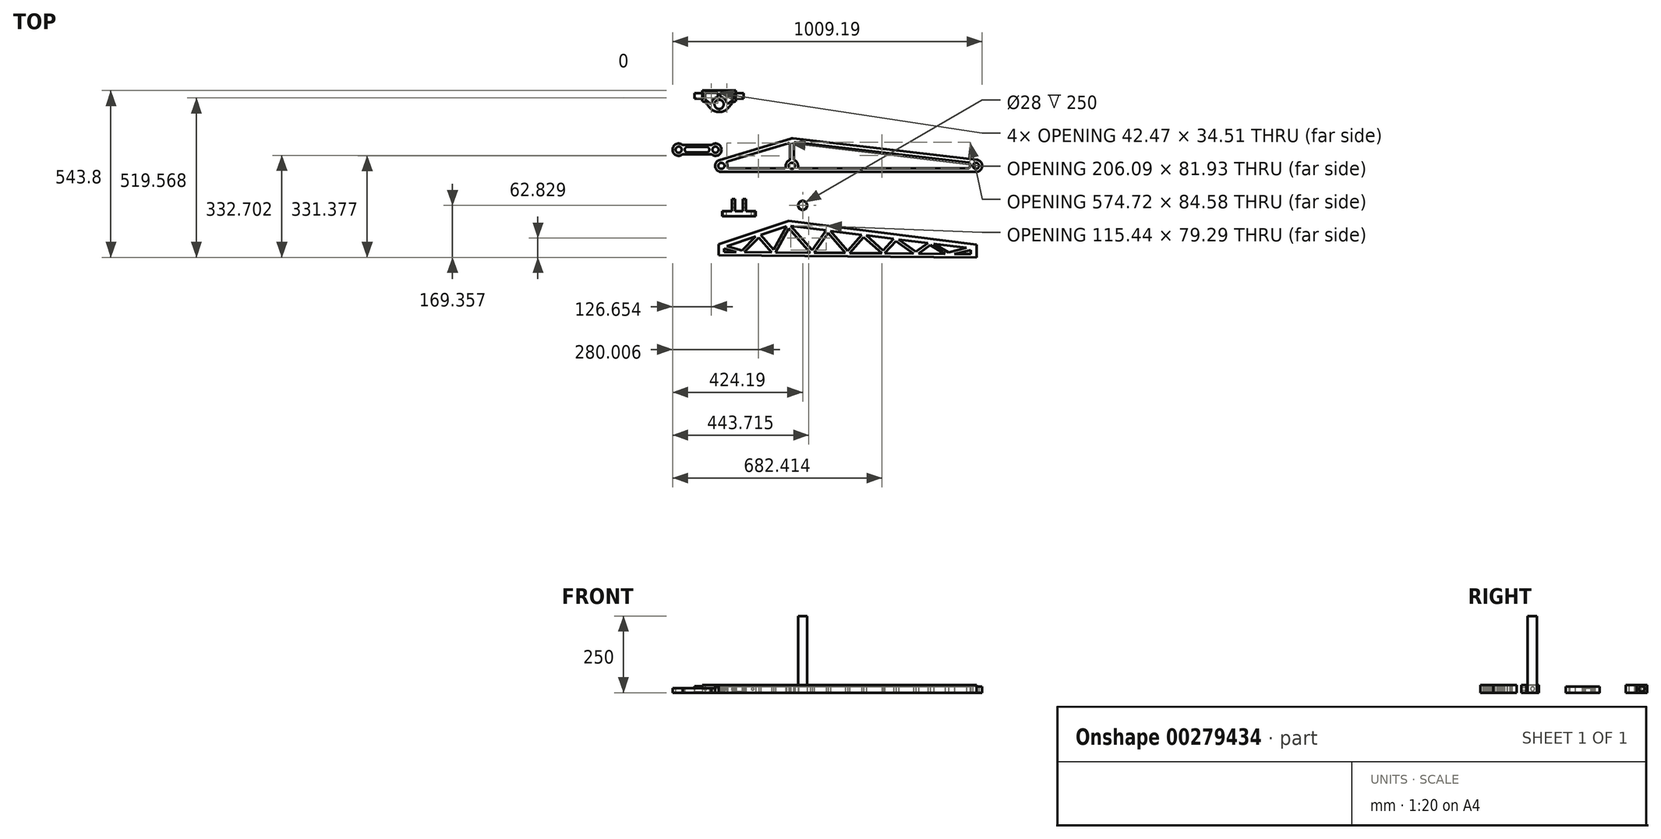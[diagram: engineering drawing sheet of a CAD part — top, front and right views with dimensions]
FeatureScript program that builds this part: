
annotation { "Feature Type Name" : "Feature", "Feature Type Description" : "" }
export const myFeature = defineFeature(function(context is Context, id is Id, definition is map)
    precondition{}
    {
        {
            var Q0;
            Q0=qCreatedBy(makeId("Top.planeOp"),FACE);
            var sketch = newSketch(context, id + "F0", { "sketchPlane" : qUnion([Q0])});
            skCircle(sketch, "E0", {"center": v(-265.14, 0) * mm, "radius": 10 * mm});
            skCircle(sketch, "E1", {"center": v(-35.14, 0) * mm, "radius": 10 * mm});
            skCircle(sketch, "E2", {"center": v(564.86, 0) * mm, "radius": 10 * mm});
            skLineSegment(sketch, "E3", {"start": v(-31.03, 89.52) * mm, "end": v(567.19, 20) * mm});
            skLineSegment(sketch, "E4", {"start": v(567.19, -20) * mm, "end": v(-265.14, -20) * mm});
            skArc(sketch, "E5", {"start": v(-265.14, -20) * mm, "mid": v(-284.92, -2.9) * mm, "end": v(-270.9, 19.15) * mm});
            skLineSegment(sketch, "E6", {"start": v(-270.9, 19.15) * mm, "end": v(-39.1, 88.81) * mm});
            skArc(sketch, "E7", {"start": v(567.19, -20) * mm, "mid": v(585, 0) * mm, "end": v(567.19, 20) * mm});
            skPoint(sketch, "E8.visualSharp", {"position": v(-35.14, 90) * mm});
            skArc(sketch, "E8.filletArc", {"start": v(-31.03, 89.52) * mm, "mid": v(-35.1, 89.58) * mm, "end": v(-39.1, 88.81) * mm});
            skLineSegment(sketch, "E9", {"start": v(-249.89, 12.94) * mm, "end": v(-41.14, 75.67) * mm});
            skLineSegment(sketch, "E10", {"start": v(-41.14, 75.67) * mm, "end": v(-249.89, 12.94) * mm});
            skLineSegment(sketch, "E11", {"start": v(-246.8, -8) * mm, "end": v(-53.47, -8) * mm});
            skLineSegment(sketch, "E12", {"start": v(-89.9, -8) * mm, "end": v(-89.9, -20) * mm, "construction": true});
            skLineSegment(sketch, "E13", {"start": v(-87.57, 61.71) * mm, "end": v(-91.02, 73.2) * mm, "construction": true});
            skLineSegment(sketch, "E14", {"start": v(-35.14, 0) * mm, "end": v(-35.14, 166.99) * mm, "construction": true});
            skLineSegment(sketch, "E15", {"start": v(-53.47, -8) * mm, "end": v(-35.14, -8) * mm, "construction": true});
            skLineSegment(sketch, "E16", {"start": v(-35.14, -8) * mm, "end": v(-16.8, -8) * mm, "construction": true});
            skLineSegment(sketch, "E17", {"start": v(-29.14, 19.08) * mm, "end": v(-29.14, 77.22) * mm});
            skLineSegment(sketch, "E18", {"start": v(-41.14, 17.52) * mm, "end": v(-29.14, 17.52) * mm, "construction": true});
            skLineSegment(sketch, "E19", {"start": v(-29.14, 77.22) * mm, "end": v(547.65, 10.19) * mm});
            skLineSegment(sketch, "E20", {"start": v(-9, 74.88) * mm, "end": v(-7.6, 86.8) * mm, "construction": true});
            skLineSegment(sketch, "E21", {"start": v(-16.8, -8) * mm, "end": v(546.53, -8) * mm});
            skArc(sketch, "E22", {"start": v(547.65, 10.19) * mm, "mid": v(544.9, 1.23) * mm, "end": v(546.53, -8) * mm});
            skArc(sketch, "E23", {"start": v(-246.8, -8) * mm, "mid": v(-245.35, 2.9) * mm, "end": v(-249.89, 12.94) * mm});
            skArc(sketch, "E24", {"start": v(-16.8, -8) * mm, "mid": v(-35.14, 20) * mm, "end": v(-53.47, -8) * mm});
            skLineSegment(sketch, "E25", {"start": v(-41.14, 75.67) * mm, "end": v(-41.14, 19.08) * mm});
            skLineSegment(sketch, "E26", {"start": v(-41.14, 40.34) * mm, "end": v(-35.14, 40.34) * mm, "construction": true});
            skLineSegment(sketch, "E27", {"start": v(-35.14, 40.34) * mm, "end": v(-29.14, 40.34) * mm, "construction": true});
            skSolve(sketch);
        }
        {
            var Q0;
            Q0 = qSketchRegion(id + "F0", true);
            extrude(context, id + "F1", {"entities" : qUnion([Q0]), "depth" : 20 * mm});
        }
        {
            var Q0;
            Q0=makeQuery(id+"F1.opExtrude","SWEPT_EDGE",EDGE,{"disambiguationData":[OSD([sQuery(id+"F0.wireOp",EDGE,"E19"),sQuery(id+"F0.wireOp",EDGE,"E22")])]});
            var Q1;
            Q1=makeQuery(id+"F1.opExtrude","SWEPT_EDGE",EDGE,{"disambiguationData":[OSD([sQuery(id+"F0.wireOp",EDGE,"E21"),sQuery(id+"F0.wireOp",EDGE,"E22")])]});
            var Q2;
            Q2=makeQuery(id+"F1.opExtrude","SWEPT_EDGE",EDGE,{"disambiguationData":[OSD([sQuery(id+"F0.wireOp",EDGE,"E17"),sQuery(id+"F0.wireOp",EDGE,"E19")])]});
            var Q3;
            Q3=makeQuery(id+"F1.opExtrude","SWEPT_EDGE",EDGE,{"disambiguationData":[OSD([sQuery(id+"F0.wireOp",EDGE,"E17"),sQuery(id+"F0.wireOp",EDGE,"E24")])]});
            var Q4;
            Q4=makeQuery(id+"F1.opExtrude","SWEPT_EDGE",EDGE,{"disambiguationData":[OSD([sQuery(id+"F0.wireOp",EDGE,"E21"),sQuery(id+"F0.wireOp",EDGE,"E24")])]});
            var Q5;
            Q5=makeQuery(id+"F1.opExtrude","SWEPT_EDGE",EDGE,{"disambiguationData":[OSD([sQuery(id+"F0.wireOp",EDGE,"E11"),sQuery(id+"F0.wireOp",EDGE,"E24")])]});
            var Q6;
            Q6=makeQuery(id+"F1.opExtrude","SWEPT_EDGE",EDGE,{"disambiguationData":[OSD([sQuery(id+"F0.wireOp",EDGE,"E24"),sQuery(id+"F0.wireOp",EDGE,"E25")])]});
            var Q7;
            Q7=makeQuery(id+"F1.opExtrude","SWEPT_EDGE",EDGE,{"disambiguationData":[OSD([sQuery(id+"F0.wireOp",EDGE,"E10"),sQuery(id+"F0.wireOp",EDGE,"E25")])]});
            var Q8;
            Q8=makeQuery(id+"F1.opExtrude","SWEPT_EDGE",EDGE,{"disambiguationData":[OSD([sQuery(id+"F0.wireOp",EDGE,"E11"),sQuery(id+"F0.wireOp",EDGE,"E23")])]});
            var Q9;
            Q9=makeQuery(id+"F1.opExtrude","SWEPT_EDGE",EDGE,{"disambiguationData":[OSD([sQuery(id+"F0.wireOp",EDGE,"E10"),sQuery(id+"F0.wireOp",EDGE,"E23")])]});
            fillet(context, id + "F2", {"entities" : qUnion([Q0, Q1, Q2, Q3, Q4, Q5, Q6, Q7, Q8, Q9]), "radius" : 5 * mm, "tangentPropagation" : true, "allowEdgeOverflow" : false});
        }
        {
            var Q0;
            Q0=qCreatedBy(makeId("Top.planeOp"),FACE);
            var sketch = newSketch(context, id + "F3", { "sketchPlane" : qUnion([Q0])});
            skLineSegment(sketch, "E28", {"start": v(-390.96, 67.67) * mm, "end": v(-297.41, 67.67) * mm});
            skLineSegment(sketch, "E29", {"start": v(-297.41, 37.67) * mm, "end": v(-390.96, 37.67) * mm});
            skArc(sketch, "E30", {"start": v(-297.41, 37.67) * mm, "mid": v(-264.19, 52.67) * mm, "end": v(-297.41, 67.67) * mm});
            skArc(sketch, "E31", {"start": v(-390.96, 67.67) * mm, "mid": v(-424.19, 52.67) * mm, "end": v(-390.96, 37.67) * mm});
            skPoint(sketch, "E32.orphan", {"position": v(-404.19, 67.67) * mm});
            skPoint(sketch, "E33.orphan", {"position": v(-404.19, 37.67) * mm});
            skPoint(sketch, "E34.orphan", {"position": v(-284.19, 37.67) * mm});
            skPoint(sketch, "E35.orphan", {"position": v(-284.19, 67.67) * mm});
            skCircle(sketch, "E36", {"center": v(-404.19, 52.67) * mm, "radius": 10 * mm});
            skCircle(sketch, "E37", {"center": v(-284.19, 52.67) * mm, "radius": 10 * mm});
            skLineSegment(sketch, "E38", {"start": v(-404.19, 52.67) * mm, "end": v(-284.19, 52.67) * mm, "construction": true});
            skLineSegment(sketch, "E39", {"start": v(-375.19, 61.67) * mm, "end": v(-313.19, 61.67) * mm});
            skArc(sketch, "E40", {"start": v(-375.19, 61.67) * mm, "mid": v(-384.19, 52.67) * mm, "end": v(-375.19, 43.67) * mm});
            skLineSegment(sketch, "E41", {"start": v(-375.19, 43.67) * mm, "end": v(-313.19, 43.67) * mm});
            skArc(sketch, "E42", {"start": v(-313.19, 61.67) * mm, "mid": v(-304.19, 52.67) * mm, "end": v(-313.19, 43.67) * mm});
            skSolve(sketch);
        }
        {
            var Q0;
            Q0 = qSketchRegion(id + "F3", true);
            extrude(context, id + "F4", {"entities" : qUnion([Q0]), "depth" : 15 * mm});
        }
        {
            var Q0;
            Q0=qCreatedBy(makeId("Top.planeOp"),FACE);
            var sketch = newSketch(context, id + "F5", { "sketchPlane" : qUnion([Q0])});
            skLineSegment(sketch, "E43", {"start": v(-327.3, 245.39) * mm, "end": v(-217.3, 245.39) * mm});
            skLineSegment(sketch, "E44", {"start": v(-217.3, 245.39) * mm, "end": v(-217.3, 210.39) * mm});
            skLineSegment(sketch, "E45", {"start": v(-327.3, 210.39) * mm, "end": v(-327.3, 245.39) * mm});
            skCircle(sketch, "E46", {"center": v(-272.3, 200.39) * mm, "radius": 15 * mm});
            skPoint(sketch, "E46.centerSnap0", {"position": v(-272.3, 175.39) * mm});
            skCircle(sketch, "E47", {"center": v(-272.3, 200.39) * mm, "radius": 25 * mm, "construction": true});
            skFitSpline(sketch, "E48", {"points": [v(-327.3, 210.39) * mm, v(-272.3, 175.39) * mm], "startDerivative": vector(60, 0) * mm, "endDerivative": vector(105, 0) * mm});
            skLineSegment(sketch, "E49", {"start": v(-272.3, 200.39) * mm, "end": v(-272.3, 245.39) * mm, "construction": true});
            skLineSegment(sketch, "E50", {"start": v(-327.3, 245.39) * mm, "end": v(-272.3, 200.39) * mm, "construction": true});
            skLineSegment(sketch, "E51", {"start": v(-272.3, 200.39) * mm, "end": v(-217.3, 245.39) * mm, "construction": true});
            skLineSegment(sketch, "E52", {"start": v(-327.3, 210.39) * mm, "end": v(-217.3, 210.39) * mm, "construction": true});
            skFitSpline(sketch, "E53.MirrorCS", {"points": [v(-217.3, 210.39) * mm, v(-272.3, 175.39) * mm], "startDerivative": vector(-60, 0) * mm, "endDerivative": vector(-105, 0) * mm});
            skLineSegment(sketch, "E54", {"start": v(-281.3, 238.41) * mm, "end": v(-313.77, 238.41) * mm});
            skLineSegment(sketch, "E55", {"start": v(-318.77, 233.41) * mm, "end": v(-318.77, 220.85) * mm});
            skLineSegment(sketch, "E56", {"start": v(-317.2, 217.2) * mm, "end": v(-304.5, 205.26) * mm});
            skArc(sketch, "E57", {"start": v(-296.27, 207.48) * mm, "mid": v(-287.26, 220.42) * mm, "end": v(-272.3, 225.39) * mm});
            skPoint(sketch, "E58.visualSharp", {"position": v(-318.77, 238.41) * mm});
            skArc(sketch, "E58.filletArc", {"start": v(-313.77, 238.41) * mm, "mid": v(-317.3, 236.95) * mm, "end": v(-318.77, 233.41) * mm});
            skPoint(sketch, "E59.visualSharp", {"position": v(-318.77, 218.69) * mm});
            skArc(sketch, "E59.filletArc", {"start": v(-318.77, 220.85) * mm, "mid": v(-318.36, 218.86) * mm, "end": v(-317.2, 217.2) * mm});
            skArc(sketch, "E60.MirrorCS", {"start": v(-230.83, 238.41) * mm, "mid": v(-227.3, 236.95) * mm, "end": v(-225.83, 233.41) * mm});
            skLineSegment(sketch, "E61.MirrorCS", {"start": v(-225.83, 233.41) * mm, "end": v(-225.83, 220.85) * mm});
            skLineSegment(sketch, "E62.MirrorCS", {"start": v(-227.4, 217.2) * mm, "end": v(-240.1, 205.26) * mm});
            skPoint(sketch, "E63.MirrorP", {"position": v(-225.83, 218.69) * mm});
            skArc(sketch, "E64.MirrorCS", {"start": v(-225.83, 220.85) * mm, "mid": v(-226.24, 218.86) * mm, "end": v(-227.4, 217.2) * mm});
            skArc(sketch, "E65.MirrorCS", {"start": v(-248.33, 207.48) * mm, "mid": v(-257.34, 220.42) * mm, "end": v(-272.3, 225.39) * mm});
            skPoint(sketch, "E66.visualSharp", {"position": v(-297.22, 198.43) * mm});
            skArc(sketch, "E66.filletArc", {"start": v(-304.5, 205.26) * mm, "mid": v(-299.76, 204.08) * mm, "end": v(-296.27, 207.48) * mm});
            skPoint(sketch, "E67.visualSharp", {"position": v(-247.38, 198.43) * mm});
            skArc(sketch, "E67.filletArc", {"start": v(-248.33, 207.48) * mm, "mid": v(-244.84, 204.08) * mm, "end": v(-240.1, 205.26) * mm});
            skLineSegment(sketch, "E68", {"start": v(-276.3, 233.41) * mm, "end": v(-276.3, 229.73) * mm});
            skPoint(sketch, "E69.orphan", {"position": v(-272.3, 238.41) * mm});
            skPoint(sketch, "E70.MirrorCS.end.orphan", {"position": v(-230.83, 238.41) * mm});
            skLineSegment(sketch, "E71.MirrorCS", {"start": v(-268.3, 233.41) * mm, "end": v(-268.3, 229.73) * mm});
            skLineSegment(sketch, "E72.MirrorCS", {"start": v(-263.3, 238.41) * mm, "end": v(-230.83, 238.41) * mm});
            skPoint(sketch, "E73.visualSharp", {"position": v(-276.3, 238.41) * mm});
            skArc(sketch, "E73.filletArc", {"start": v(-276.3, 233.41) * mm, "mid": v(-277.76, 236.95) * mm, "end": v(-281.3, 238.41) * mm});
            skPoint(sketch, "E74.visualSharp", {"position": v(-268.3, 238.41) * mm});
            skArc(sketch, "E74.filletArc", {"start": v(-263.3, 238.41) * mm, "mid": v(-266.84, 236.95) * mm, "end": v(-268.3, 233.41) * mm});
            skArc(sketch, "E75", {"start": v(-280.37, 224.05) * mm, "mid": v(-277.42, 226.24) * mm, "end": v(-276.3, 229.73) * mm});
            skPoint(sketch, "E76.orphan", {"position": v(-276.3, 225.07) * mm});
            skArc(sketch, "E77.MirrorCS", {"start": v(-264.23, 224.05) * mm, "mid": v(-267.18, 226.24) * mm, "end": v(-268.3, 229.73) * mm});
            skPoint(sketch, "E78.orphan", {"position": v(-268.3, 225.07) * mm});
            skSolve(sketch);
        }
        {
            var Q0;
            Q0 = qSketchRegion(id + "F5", true);
            extrude(context, id + "F6", {"entities" : qUnion([Q0]), "depth" : 25 * mm});
        }
        {
            var Q0;
            Q0=makeQuery(id+"F6.opExtrude","SWEPT_FACE",FACE,{"disambiguationData":[OSD([sQuery(id+"F5.wireOp",EDGE,"E45")])]});
            var sketch = newSketch(context, id + "F7", { "sketchPlane" : qUnion([Q0])});
            skCircle(sketch, "E79", {"center": v(-227.89, 12.5) * mm, "radius": 9 * mm});
            skPoint(sketch, "E79.centerSnap0", {"position": v(-227.89, 25) * mm});
            skPoint(sketch, "E79.centerSnap1", {"position": v(-245.39, 12.5) * mm});
            skSolve(sketch);
        }
        {
            var Q0;
            Q0 = qSketchRegion(id + "F7", true);
            extrude(context, id + "F8", {"entities" : qUnion([Q0]), "operationType" : NewBodyOperationType.ADD, "depth" : 25 * mm});
        }
        {
            var Q0;
            Q0=makeQuery(id+"F6.opExtrude","CAP_EDGE",EDGE,{"disambiguationData":[OSD([sQuery(id+"F5.wireOp",EDGE,"E43")])],"isStart":false});
            cPoint(context, id + "F9", {"entities" : qUnion([Q0]), "parameter" : 0.5});
        }
        {
            var Q0;
            Q0 = qCreatedBy(id + "F9" ,VERTEX);
            var Q1;
            Q1=makeQuery(id+"F6.opExtrude","CAP_EDGE",EDGE,{"disambiguationData":[OSD([sQuery(id+"F5.wireOp",EDGE,"E43")])],"isStart":false});
            cPlane(context, id + "F10", {"entities" : qUnion([Q0, Q1]), "cplaneType" : CPlaneType.LINE_POINT, "offset" : 25 * mm, "width" : 150 * mm, "height" : 150 * mm});
        }
        {
            var Q0;
            Q0=makeQuery(id+"F6.opExtrude","SWEPT_BODY",BODY,{"disambiguationData":[OSD([sQuery(id+"F5.wireOp",EDGE,"E43"),sQuery(id+"F5.wireOp",EDGE,"E44"),sQuery(id+"F5.wireOp",EDGE,"SvP0zgxu-rB9L-MZa4-3J7w-tIJTC1WoX9Vp"),sQuery(id+"F5.wireOp",EDGE,"GX9iZxod-qHFo-fape-ixxr-I3ToKnoXxPaa"),sQuery(id+"F5.wireOp",EDGE,"SmAqcUY8-qOSf-tAji-bSFe-nhmfK1cs2rVA"),sQuery(id+"F5.wireOp",EDGE,"E45"),sQuery(id+"F5.wireOp",EDGE,"E46")])]});
            var Q1;
            Q1=qCreatedBy(id+"F10.planeOp",FACE);
            mirror(context, id + "F11", {"operationType" : NewBodyOperationType.ADD, "entities" : qUnion([Q0]), "mirrorPlane" : qUnion([Q1])});
        }
        {
            var Q0;
            Q0=qCreatedBy(makeId("Top.planeOp"),FACE);
            var sketch = newSketch(context, id + "F12", { "sketchPlane" : qUnion([Q0])});
            skLineSegment(sketch, "E80", {"start": v(-262.79, -164.9) * mm, "end": v(-262.79, -148.19) * mm});
            skLineSegment(sketch, "E81", {"start": v(-262.79, -148.19) * mm, "end": v(-230.29, -148.19) * mm});
            skLineSegment(sketch, "E82", {"start": v(-230.29, -148.19) * mm, "end": v(-230.29, -108.19) * mm});
            skLineSegment(sketch, "E83", {"start": v(-230.29, -108.19) * mm, "end": v(-220.29, -108.19) * mm});
            skLineSegment(sketch, "E84", {"start": v(-220.29, -108.19) * mm, "end": v(-220.29, -148.19) * mm});
            skLineSegment(sketch, "E85", {"start": v(-220.29, -148.19) * mm, "end": v(-207.79, -148.19) * mm});
            skLineSegment(sketch, "E86", {"start": v(-207.79, -148.19) * mm, "end": v(-207.79, -164.9) * mm});
            skLineSegment(sketch, "E87", {"start": v(-207.79, -164.9) * mm, "end": v(-262.79, -164.9) * mm});
            skLineSegment(sketch, "E88.MirrorCS", {"start": v(-195.29, -148.19) * mm, "end": v(-207.79, -148.19) * mm});
            skLineSegment(sketch, "E89.MirrorCS", {"start": v(-152.79, -164.9) * mm, "end": v(-152.79, -148.19) * mm});
            skLineSegment(sketch, "E90.MirrorCS", {"start": v(-185.29, -108.19) * mm, "end": v(-195.29, -108.19) * mm});
            skLineSegment(sketch, "E91.MirrorCS", {"start": v(-195.29, -108.19) * mm, "end": v(-195.29, -148.19) * mm});
            skLineSegment(sketch, "E92.MirrorCS", {"start": v(-185.29, -148.19) * mm, "end": v(-185.29, -108.19) * mm});
            skLineSegment(sketch, "E93.MirrorCS", {"start": v(-152.79, -148.19) * mm, "end": v(-185.29, -148.19) * mm});
            skLineSegment(sketch, "E94.MirrorCS", {"start": v(-207.79, -164.9) * mm, "end": v(-152.79, -164.9) * mm});
            skSolve(sketch);
        }
        {
            var Q0;
            Q0=makeQuery(id+"F12.imprint","IMPRINT",FACE,{"disambiguationData":[TD([[makeQuery(id+"F12.imprint","IMPRINT",EDGE,{"derivedFrom":sQuery(id+"F12.wireOp",EDGE,"E80")}),-1.0]])]});
            var Q1;
            Q1=makeQuery(id+"F12.imprint","IMPRINT",FACE,{"disambiguationData":[TD([[makeQuery(id+"F12.imprint","IMPRINT",EDGE,{"derivedFrom":sQuery(id+"F12.wireOp",EDGE,"E86")}),1.0]])]});
            extrude(context, id + "F13", {"entities" : qUnion([Q0, Q1]), "depth" : 25 * mm});
        }
        {
            var Q0;
            Q0=makeQuery(id+"F13.opExtrude","SWEPT_FACE",FACE,{"disambiguationData":[OSD([sQuery(id+"F12.wireOp",EDGE,"E92.MirrorCS")])]});
            var sketch = newSketch(context, id + "F14", { "sketchPlane" : qUnion([Q0])});
            skCircle(sketch, "E95", {"center": v(-128.19, 12.5) * mm, "radius": 6.36 * mm});
            skPoint(sketch, "E96", {"position": v(-108.19, 12.5) * mm});
            skPoint(sketch, "E97", {"position": v(-128.19, 25) * mm});
            skSolve(sketch);
        }
        {
            var Q0;
            Q0=makeQuery(id+"F14.imprint","IMPRINT",FACE,{"disambiguationData":[TD([[makeQuery(id+"F14.imprint","IMPRINT",EDGE,{"derivedFrom":sQuery(id+"F14.wireOp",EDGE,"E95")}),1.0]])]});
            extrude(context, id + "F15", {"entities" : qUnion([Q0]), "operationType" : NewBodyOperationType.REMOVE, "endBound" : BoundingType.THROUGH_ALL, "oppositeDirection" : true, "depth" : 25 * mm});
        }
        {
            var Q0;
            Q0=makeQuery(id+"F13.opExtrude","SWEPT_FACE",FACE,{"disambiguationData":[OSD([sQuery(id+"F12.wireOp",EDGE,"E93.MirrorCS")])]});
            var sketch = newSketch(context, id + "F16", { "sketchPlane" : qUnion([Q0])});
            skCircle(sketch, "E98", {"center": v(162.79, 12.5) * mm, "radius": 4.25 * mm});
            skPoint(sketch, "E98.centerSnap0", {"position": v(152.79, 12.5) * mm});
            skLineSegment(sketch, "E99", {"start": v(207.79, 25) * mm, "end": v(207.79, 0) * mm, "construction": true});
            skCircle(sketch, "E100.MirrorC", {"center": v(252.79, 12.5) * mm, "radius": 4.25 * mm});
            skSolve(sketch);
        }
        {
            var Q0;
            Q0 = qSketchRegion(id + "F16", true);
            extrude(context, id + "F17", {"entities" : qUnion([Q0]), "operationType" : NewBodyOperationType.REMOVE, "endBound" : BoundingType.THROUGH_ALL, "oppositeDirection" : true, "depth" : 25 * mm});
        }
        {
            var Q0;
            Q0=makeQuery(id+"F6.opExtrude","SWEPT_FACE",FACE,{"disambiguationData":[OSD([sQuery(id+"F5.wireOp",EDGE,"E43")])]});
            var sketch = newSketch(context, id + "F18", { "sketchPlane" : qUnion([Q0])});
            skCircle(sketch, "E101", {"center": v(317.3, 12.5) * mm, "radius": 4.6 * mm});
            skPoint(sketch, "E101.centerSnap0", {"position": v(327.3, 12.5) * mm});
            skLineSegment(sketch, "E102", {"start": v(272.3, 25) * mm, "end": v(272.3, 0) * mm});
            skCircle(sketch, "E103.MirrorC", {"center": v(227.3, 12.5) * mm, "radius": 4.6 * mm});
            skSolve(sketch);
        }
        {
            var Q0;
            Q0 = qSketchRegion(id + "F18", true);
            extrude(context, id + "F19", {"entities" : qUnion([Q0]), "operationType" : NewBodyOperationType.REMOVE, "oppositeDirection" : true, "depth" : 20 * mm});
        }
        {
            assignVariable(context, id + "F20", {"name" : "neck", "anyValue" : 200});
        }
        {
            var Q0;
            Q0=qCreatedBy(makeId("Top.planeOp"),FACE);
            var sketch = newSketch(context, id + "F21", { "sketchPlane" : qUnion([Q0])});
            skCircle(sketch, "E104", {"center": v(0, -129.05) * mm, "radius": 15 * mm});
            skCircle(sketch, "E105", {"center": v(0, -129.05) * mm, "radius": 14 * mm});
            skSolve(sketch);
        }
        {
            var Q0;
            Q0=makeQuery(id+"F21.imprint","IMPRINT",FACE,{"disambiguationData":[TD([[makeQuery(id+"F21.imprint","IMPRINT",EDGE,{"derivedFrom":sQuery(id+"F21.wireOp",EDGE,"E104")}),1.0]])]});
            extrude(context, id + "F22", {"entities" : qUnion([Q0]), "depth" : (getVariable(context, 'neck') + 50) * mm});
        }
        {
            var Q0;
            Q0=qCreatedBy(makeId("Top.planeOp"),FACE);
            var sketch = newSketch(context, id + "F23", { "sketchPlane" : qUnion([Q0])});
            skLineSegment(sketch, "E106", {"start": v(-273.3, -255.7) * mm, "end": v(-45.66, -179.82) * mm});
            skLineSegment(sketch, "E107", {"start": v(-45.66, -179.82) * mm, "end": v(567.02, -256.65) * mm});
            skLineSegment(sketch, "E108", {"start": v(567.02, -256.65) * mm, "end": v(567.02, -298.4) * mm});
            skLineSegment(sketch, "E109", {"start": v(567.02, -298.4) * mm, "end": v(-273.3, -290.84) * mm});
            skLineSegment(sketch, "E110", {"start": v(-273.3, -290.84) * mm, "end": v(-273.3, -255.7) * mm});
            skLineSegment(sketch, "E111", {"start": v(-38.2, -195.93) * mm, "end": v(77.25, -210.4) * mm});
            skLineSegment(sketch, "E112", {"start": v(548.46, -274.63) * mm, "end": v(548.46, -287.94) * mm});
            skLineSegment(sketch, "E113", {"start": v(548.46, -287.94) * mm, "end": v(494.87, -287.46) * mm});
            skLineSegment(sketch, "E114", {"start": v(-256.21, -280.7) * mm, "end": v(-256.21, -270.36) * mm});
            skLineSegment(sketch, "E115", {"start": v(-247.62, -262.32) * mm, "end": v(-152.92, -230.75) * mm});
            skLineSegment(sketch, "E116", {"start": v(-45.66, -195) * mm, "end": v(31.54, -283.29) * mm, "construction": true});
            skLineSegment(sketch, "E117", {"start": v(31.54, -283.29) * mm, "end": v(82.88, -211.12) * mm, "construction": true});
            skLineSegment(sketch, "E118", {"start": v(82.88, -211.12) * mm, "end": v(146.12, -284.32) * mm, "construction": true});
            skLineSegment(sketch, "E119", {"start": v(146.12, -284.32) * mm, "end": v(198.68, -225.64) * mm, "construction": true});
            skLineSegment(sketch, "E120", {"start": v(198.68, -225.64) * mm, "end": v(263.05, -283.29) * mm, "construction": true});
            skLineSegment(sketch, "E121", {"start": v(263.05, -283.29) * mm, "end": v(302.97, -238.71) * mm, "construction": true});
            skLineSegment(sketch, "E122", {"start": v(302.97, -238.71) * mm, "end": v(369.5, -286.33) * mm, "construction": true});
            skLineSegment(sketch, "E123", {"start": v(369.5, -286.33) * mm, "end": v(415, -252.76) * mm, "construction": true});
            skLineSegment(sketch, "E124", {"start": v(415, -252.76) * mm, "end": v(474.17, -287.27) * mm, "construction": true});
            skLineSegment(sketch, "E125", {"start": v(474.17, -287.27) * mm, "end": v(548.46, -269.5) * mm, "construction": true});
            skLineSegment(sketch, "E126", {"start": v(-45.66, -195) * mm, "end": v(-94.21, -282.15) * mm, "construction": true});
            skLineSegment(sketch, "E127", {"start": v(-94.21, -282.15) * mm, "end": v(-142.26, -227.2) * mm, "construction": true});
            skLineSegment(sketch, "E128", {"start": v(-142.26, -227.2) * mm, "end": v(-196.56, -281.23) * mm, "construction": true});
            skLineSegment(sketch, "E129", {"start": v(-196.56, -281.23) * mm, "end": v(-256.21, -265.18) * mm, "construction": true});
            skLineSegment(sketch, "E130.0", {"start": v(-198.05, -275.65) * mm, "end": v(-247.62, -262.32) * mm});
            skLineSegment(sketch, "E130.1", {"start": v(-152.92, -230.75) * mm, "end": v(-198.05, -275.65) * mm});
            skLineSegment(sketch, "E130.2", {"start": v(-95.12, -273.51) * mm, "end": v(-137.12, -225.48) * mm});
            skLineSegment(sketch, "E130.3", {"start": v(-52.68, -197.34) * mm, "end": v(-95.12, -273.51) * mm});
            skLineSegment(sketch, "E130.4", {"start": v(313.39, -240.02) * mm, "end": v(369.46, -280.15) * mm});
            skLineSegment(sketch, "E130.5", {"start": v(369.46, -280.15) * mm, "end": v(407.8, -251.86) * mm});
            skLineSegment(sketch, "E130.6", {"start": v(427.64, -254.34) * mm, "end": v(474.96, -281.94) * mm});
            skLineSegment(sketch, "E130.7", {"start": v(474.96, -281.94) * mm, "end": v(534.36, -267.73) * mm});
            skLineSegment(sketch, "E130.8", {"start": v(262.66, -276.23) * mm, "end": v(296.94, -237.96) * mm});
            skLineSegment(sketch, "E130.9", {"start": v(207.4, -226.73) * mm, "end": v(262.66, -276.23) * mm});
            skLineSegment(sketch, "E130.10", {"start": v(146.2, -276.75) * mm, "end": v(192.65, -224.88) * mm});
            skLineSegment(sketch, "E130.11", {"start": v(90.3, -212.04) * mm, "end": v(146.2, -276.75) * mm});
            skLineSegment(sketch, "E130.12", {"start": v(31.13, -275.23) * mm, "end": v(77.25, -210.4) * mm});
            skLineSegment(sketch, "E130.13", {"start": v(-38.2, -195.93) * mm, "end": v(31.13, -275.23) * mm});
            skLineSegment(sketch, "E131.0", {"start": v(-216.47, -281.05) * mm, "end": v(-256.21, -270.36) * mm});
            skLineSegment(sketch, "E131.1", {"start": v(-142.51, -234.5) * mm, "end": v(-189.54, -281.3) * mm});
            skLineSegment(sketch, "E131.2", {"start": v(-100.9, -282.1) * mm, "end": v(-142.51, -234.5) * mm});
            skLineSegment(sketch, "E131.3", {"start": v(-44.75, -203.64) * mm, "end": v(-88.52, -282.2) * mm});
            skLineSegment(sketch, "E131.4", {"start": v(303.7, -245.39) * mm, "end": v(360.8, -286.25) * mm});
            skLineSegment(sketch, "E131.5", {"start": v(377.83, -286.4) * mm, "end": v(415.33, -258.74) * mm});
            skLineSegment(sketch, "E131.6", {"start": v(415.33, -258.74) * mm, "end": v(464.1, -287.18) * mm});
            skLineSegment(sketch, "E131.7", {"start": v(494.87, -287.46) * mm, "end": v(548.46, -274.63) * mm});
            skLineSegment(sketch, "E131.8", {"start": v(267.85, -285.42) * mm, "end": v(303.7, -245.39) * mm});
            skLineSegment(sketch, "E131.9", {"start": v(199.07, -232.7) * mm, "end": v(257.83, -285.32) * mm});
            skLineSegment(sketch, "E131.10", {"start": v(152.78, -284.38) * mm, "end": v(199.07, -232.7) * mm});
            skLineSegment(sketch, "E131.11", {"start": v(83.26, -219.2) * mm, "end": v(139.46, -284.26) * mm});
            skLineSegment(sketch, "E131.12", {"start": v(37.63, -283.34) * mm, "end": v(83.26, -219.2) * mm});
            skLineSegment(sketch, "E131.13", {"start": v(-44.75, -203.64) * mm, "end": v(24.84, -283.23) * mm});
            skLineSegment(sketch, "E132.trimOffspring", {"start": v(-137.12, -225.48) * mm, "end": v(-52.68, -197.34) * mm});
            skLineSegment(sketch, "E133.trimOffspring", {"start": v(-216.47, -281.05) * mm, "end": v(-256.21, -280.7) * mm});
            skLineSegment(sketch, "E134.trimOffspring", {"start": v(-100.9, -282.1) * mm, "end": v(-189.54, -281.3) * mm});
            skLineSegment(sketch, "E135.trimOffspring", {"start": v(24.84, -283.23) * mm, "end": v(-88.52, -282.2) * mm});
            skLineSegment(sketch, "E136.trimOffspring", {"start": v(90.3, -212.04) * mm, "end": v(192.65, -224.88) * mm});
            skLineSegment(sketch, "E137.trimOffspring", {"start": v(139.46, -284.26) * mm, "end": v(37.63, -283.34) * mm});
            skLineSegment(sketch, "E138.trimOffspring", {"start": v(207.4, -226.73) * mm, "end": v(296.94, -237.96) * mm});
            skLineSegment(sketch, "E139.trimOffspring", {"start": v(257.83, -285.32) * mm, "end": v(152.78, -284.38) * mm});
            skLineSegment(sketch, "E140.trimOffspring", {"start": v(360.8, -286.25) * mm, "end": v(267.85, -285.42) * mm});
            skLineSegment(sketch, "E141.trimOffspring", {"start": v(313.39, -240.02) * mm, "end": v(407.8, -251.86) * mm});
            skLineSegment(sketch, "E142.trimOffspring", {"start": v(427.64, -254.34) * mm, "end": v(534.36, -267.73) * mm});
            skLineSegment(sketch, "E143.trimOffspring", {"start": v(464.1, -287.18) * mm, "end": v(377.83, -286.4) * mm});
            skSolve(sketch);
        }
        {
            var Q0;
            Q0=makeQuery(id+"F23.imprint","IMPRINT",FACE,{"disambiguationData":[TD([[makeQuery(id+"F23.imprint","IMPRINT",EDGE,{"derivedFrom":sQuery(id+"F23.wireOp",EDGE,"E106")}),-1.0]])]});
            extrude(context, id + "F24", {"entities" : qUnion([Q0]), "depth" : 25 * mm});
        }
    });
